# Revit family: 206_VAM-_
name_source: partatom
category: Duct Accessories
units: mm (PartAtom-declared; Revit-internal decimal feet)

## family parameters
Always vertical = Yes
Cut with Voids When Loaded = No
Part Type = Breaks Into
Round Connector Dimension = Use Diameter
Shared = No
Work Plane-Based = No

## types (4) — shared parameters
Description = Damper plenum box
Manufacturer = Climecon
QmdConnectorList = 201;D;202;D
URL = www.climecon.fi
magiPartTypeId = 206
magiProductFamilyId = VAM-*
zero-valued in all types: MC_Default_elevation

## per-type parameters (varying)
| type | CB | CH | CH__ve | D | H2 | H2D | L2 | L2D | W2D | X |
| VAM-100 | 250 mm  [stored 0.82021 ft] | 125 mm  [stored 0.410105 ft] | -125 mm  [stored -0.410105 ft] | 100 mm | 63 mm | 125 mm  [stored 0.410105 ft] | 115 mm  [stored 0.377297 ft] | 230 mm  [stored 0.754593 ft] | 250 mm  [stored 0.82021 ft] | 98 mm  [stored 0.321522 ft] |
| VAM-200 | 450 mm  [stored 1.47638 ft] | 225 mm  [stored 0.738189 ft] | -225 mm  [stored -0.738189 ft] | 200 mm | 113 mm | 225 mm  [stored 0.738189 ft] | 215 mm  [stored 0.705381 ft] | 430 mm | 450 mm  [stored 1.47638 ft] | 145 mm  [stored 0.475722 ft] |
| VAM-160 | 370 mm  [stored 1.21391 ft] | 185 mm  [stored 0.606955 ft] | -185 mm  [stored -0.606955 ft] | 160 mm | 93 mm | 185 mm  [stored 0.606955 ft] | 175 mm  [stored 0.574147 ft] | 350 mm | 370 mm  [stored 1.21391 ft] | 125 mm  [stored 0.410105 ft] |
| VAM-125 | 300 mm  [stored 0.984252 ft] | 150 mm  [stored 0.492126 ft] | -150 mm  [stored -0.492126 ft] | 125 mm | 75 mm  [stored 0.246063 ft] | 150 mm  [stored 0.492126 ft] | 140 mm  [stored 0.459318 ft] | 280 mm | 300 mm  [stored 0.984252 ft] | 115 mm  [stored 0.377297 ft] |

note: column(s) folded — value = type name in every type: magiProductCode, magiProductId

note: [stored X ft] marks values corroborated as IEEE doubles in the binary element streams (Revit-internal decimal feet)

## geometry (parser evidence)
native form markers: Sweep x2
no freeform markers — native parametric forms only
